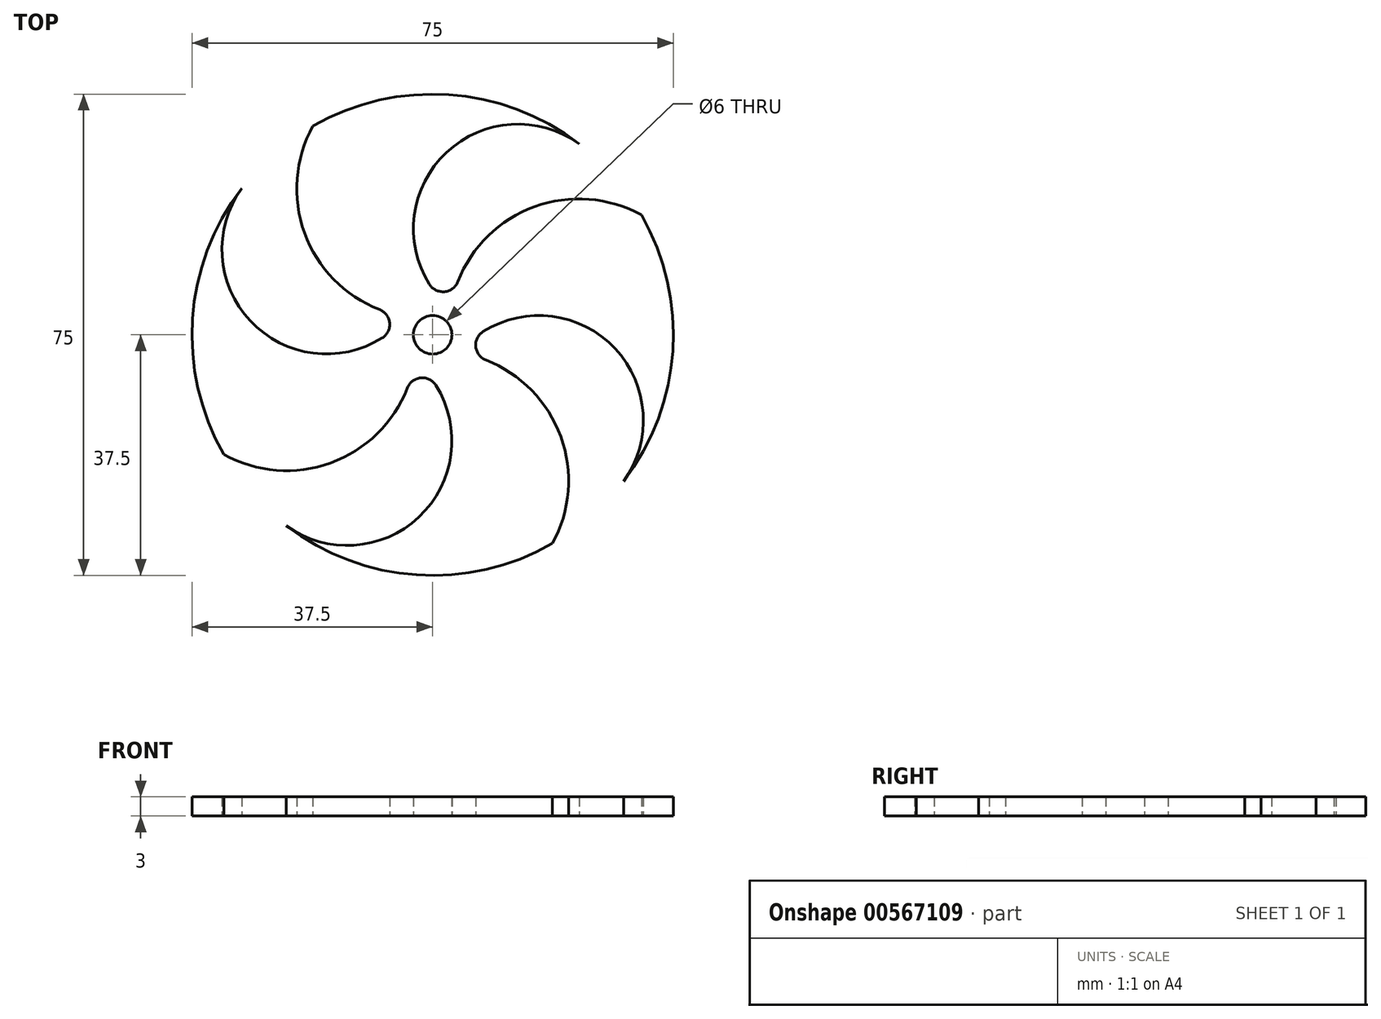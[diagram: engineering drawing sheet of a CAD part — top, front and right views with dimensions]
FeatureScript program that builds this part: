
annotation { "Feature Type Name" : "Feature", "Feature Type Description" : "" }
export const myFeature = defineFeature(function(context is Context, id is Id, definition is map)
    precondition{}
    {
        {
            var Q0;
            Q0=qCreatedBy(makeId("Top.planeOp"),FACE);
            var sketch = newSketch(context, id + "F0", { "sketchPlane" : qUnion([Q0])});
            skLineSegment(sketch, "E0.bottom", {"start": v(0, 0) * mm, "end": v(75, 0) * mm, "construction": true});
            skLineSegment(sketch, "E0.top", {"start": v(0, -75) * mm, "end": v(75, -75) * mm, "construction": true});
            skLineSegment(sketch, "E0.left", {"start": v(0, 0) * mm, "end": v(0, -75) * mm, "construction": true});
            skLineSegment(sketch, "E0.right", {"start": v(75, 0) * mm, "end": v(75, -75) * mm, "construction": true});
            skLineSegment(sketch, "E1", {"start": v(0, -75) * mm, "end": v(75, 0) * mm, "construction": true});
            skCircle(sketch, "E2", {"center": v(37.5, -37.5) * mm, "radius": 3 * mm});
            skCircle(sketch, "E3", {"center": v(37.5, -37.5) * mm, "radius": 37.5 * mm});
            skArc(sketch, "E4", {"start": v(66.17, -61.67) * mm, "mid": v(66.5, -40.3) * mm, "end": v(45.37, -37) * mm});
            skArc(sketch, "E5", {"start": v(56.17, -70.02) * mm, "mid": v(57.47, -53.38) * mm, "end": v(45.8, -41.44) * mm});
            skPoint(sketch, "E6.visualSharp", {"position": v(41.56, -40.3) * mm});
            skArc(sketch, "E6.filletArc", {"start": v(45.37, -37) * mm, "mid": v(44.21, -39.35) * mm, "end": v(45.8, -41.44) * mm});
            skArc(sketch, "E7.1.0", {"start": v(61.67, -8.83) * mm, "mid": v(40.3, -8.5) * mm, "end": v(37, -29.63) * mm});
            skArc(sketch, "E7.1.1", {"start": v(37, -29.63) * mm, "mid": v(39.35, -30.79) * mm, "end": v(41.44, -29.2) * mm});
            skArc(sketch, "E7.1.2", {"start": v(70.02, -18.83) * mm, "mid": v(53.38, -17.53) * mm, "end": v(41.44, -29.2) * mm});
            skArc(sketch, "E7.2.0", {"start": v(8.83, -13.33) * mm, "mid": v(8.5, -34.7) * mm, "end": v(29.63, -38) * mm});
            skArc(sketch, "E7.2.1", {"start": v(29.63, -38) * mm, "mid": v(30.79, -35.65) * mm, "end": v(29.2, -33.56) * mm});
            skArc(sketch, "E7.2.2", {"start": v(18.83, -4.98) * mm, "mid": v(17.53, -21.62) * mm, "end": v(29.2, -33.56) * mm});
            skArc(sketch, "E7.3.0", {"start": v(13.33, -66.17) * mm, "mid": v(34.7, -66.5) * mm, "end": v(38, -45.37) * mm});
            skArc(sketch, "E7.3.1", {"start": v(38, -45.37) * mm, "mid": v(35.65, -44.21) * mm, "end": v(33.56, -45.8) * mm});
            skArc(sketch, "E7.3.2", {"start": v(4.98, -56.17) * mm, "mid": v(21.62, -57.47) * mm, "end": v(33.56, -45.8) * mm});
            skSolve(sketch);
        }
        {
            var Q0;
            Q0=makeQuery(id+"F0.imprint","IMPRINT",FACE,{"disambiguationData":[TD([[makeQuery(id+"F0.imprint","IMPRINT",EDGE,{"derivedFrom":sQuery(id+"F0.wireOp",EDGE,"E2")}),-1.0]])]});
            extrude(context, id + "F1", {"entities" : qUnion([Q0]), "depth" : 3 * mm, "offsetDistance" : 25 * mm});
        }
    });
